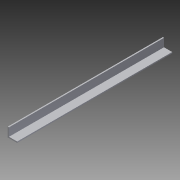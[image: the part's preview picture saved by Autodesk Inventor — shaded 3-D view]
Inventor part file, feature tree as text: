
AUTODESK INVENTOR PART (.ipt)
format: ipt  version: 2014 SP1 (Build 180222100, 222)  size: 74,752 bytes
history: native  units: in
note: dims shown in document units (in); Inventor stores cm internally (conversion verified against a paired STEP export)
features: extrude x1, sketch x1
ambient origin geometry x8: Origin, YZ Plane, XZ Plane, XY Plane, X Axis, Y Axis, Z Axis, Center Point
bodies: Solid1 (feature_tree)
feature tree (2):
  extrude  "Extrusion1"  Depth=0.0625in
  sketch  "Sketch1"  dims[d0=0.5in d1=0.0625in d2=0.5in d3=0.0625in d4=8.25in d5=0.0in]
